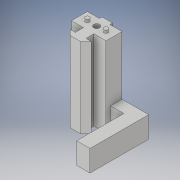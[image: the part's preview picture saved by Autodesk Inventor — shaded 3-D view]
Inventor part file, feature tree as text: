
AUTODESK INVENTOR PART (.ipt)
format: ipt  version: 2018 (Build 220112000, 112)  size: 160,768 bytes
history: native  units: in
note: dims shown in document units (in); Inventor stores cm internally (conversion verified against a paired STEP export)
features: sketch x6, extrude x5, hole x1
ambient origin geometry x8: Origin, YZ Plane, XZ Plane, XY Plane, X Axis, Y Axis, Z Axis, Center Point
bodies: Solid1 (feature_tree)
feature tree (12):
  extrude  "Extrusion1"  Depth=0.3in
  extrude  "Extrusion2"  Depth=0.25in
  extrude  "Extrusion3"  Depth=0.05in
  hole  "Hole1"  [1 undecoded]
  extrude  "Extrusion4"  Depth=0.1in
  sketch  "Sketch8"  dims[d10=1.5in d11=0.0in d12=0.15in d14=0.08in d18=0.05in d19=0.0in d20=0.15in d21=0.08in d22=0.05in d23=0.0in d24=0.325in d25=0.11in d26=0.11in d27=0.75in d28=0.375in d29=0.25in d30=0.5635in d31=0.45in d32=0.8108in d33=0.215in d34=0.4in d35=0.5in d36=0.0in d39=0.885in d40=0.0in]
  extrude  "Extrusion5"  Depth=0.15in
  sketch  "Sketch1"  dims[d0=0.65in d1=0.3in]
  sketch  "Sketch2"  dims[d2=0.1in d3=0.25in]
  sketch  "Sketch3"  dims[d4=0.2in d5=0.05in]
  sketch  "Sketch6"  dims[d6=0.1in d7=0.1in]
  sketch  "Sketch7"  dims[d8=0.1in d9=0.1in]
note: 1 required parameter value undecoded (feature->parameter linkage not recoverable at this tier; creation-order binding heuristic only, values carry confidence <= 0.55)
